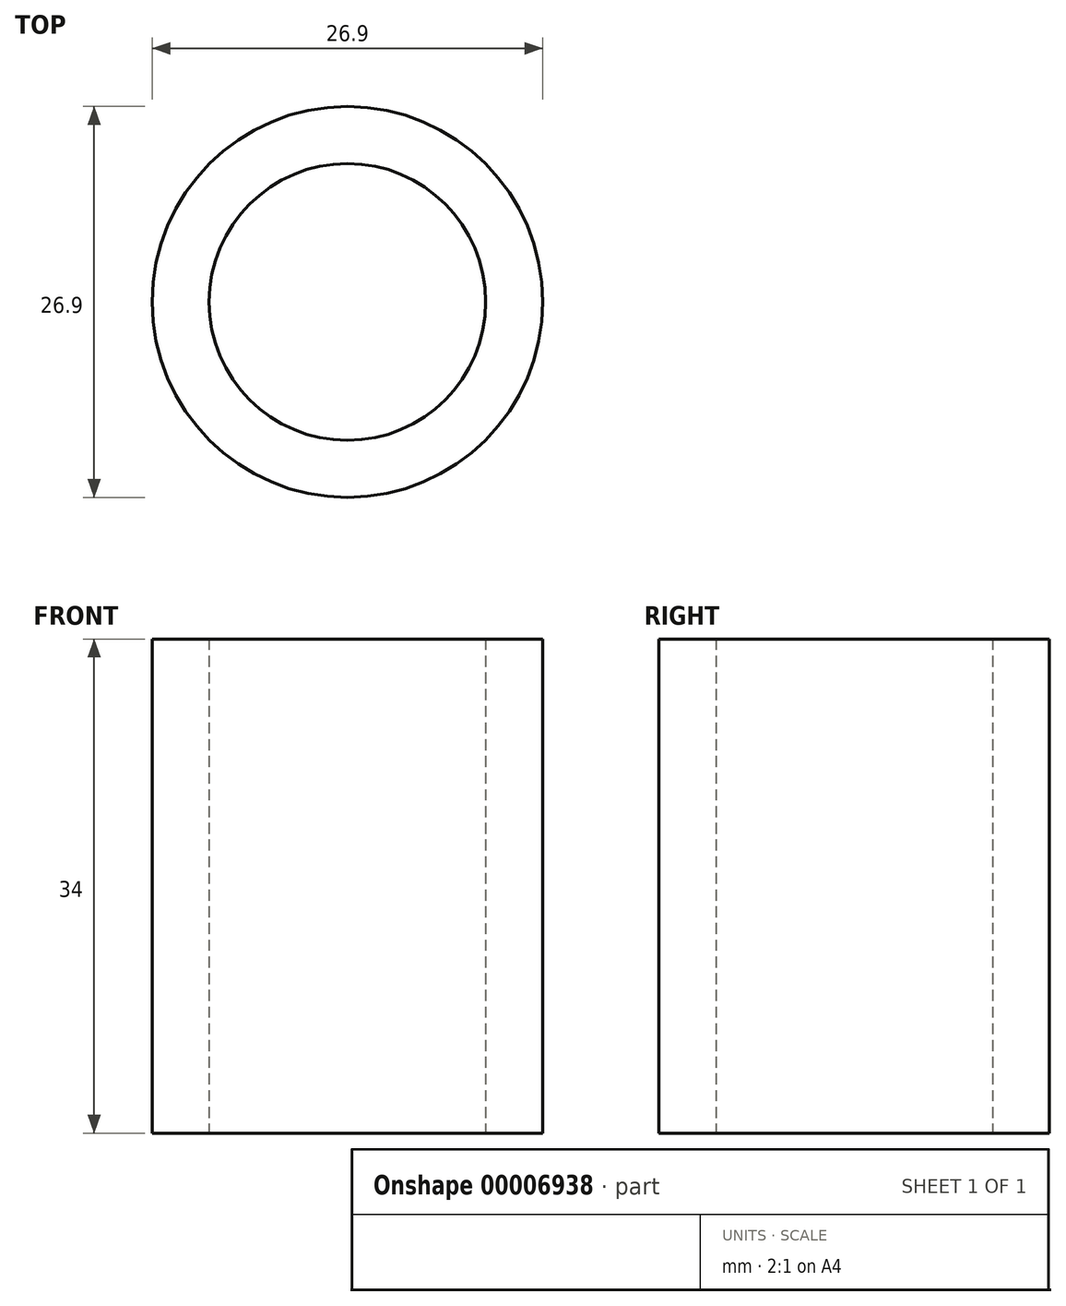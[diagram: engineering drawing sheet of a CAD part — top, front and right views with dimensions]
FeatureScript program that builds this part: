
annotation { "Feature Type Name" : "Feature", "Feature Type Description" : "" }
export const myFeature = defineFeature(function(context is Context, id is Id, definition is map)
    precondition{}
    {
        {
            var Q0;
            Q0=qCreatedBy(makeId("Top.planeOp"),FACE);
            var sketch = newSketch(context, id + "F0", { "sketchPlane" : qUnion([Q0])});
            skCircle(sketch, "E0", {"center": v(0, 0) * mm, "radius": 13.45 * mm});
            skCircle(sketch, "E1", {"center": v(0, 0) * mm, "radius": 9.53 * mm});
            skSolve(sketch);
        }
        {
            var Q0;
            Q0=makeQuery(id+"F0.imprint","IMPRINT",FACE,{"disambiguationData":[TD([[makeQuery(id+"F0.imprint","IMPRINT",EDGE,{"derivedFrom":sQuery(id+"F0.wireOp",EDGE,"E0")}),1.0]])]});
            extrude(context, id + "F1", {"entities" : qUnion([Q0]), "depth" : (34) * mm});
        }
    });
